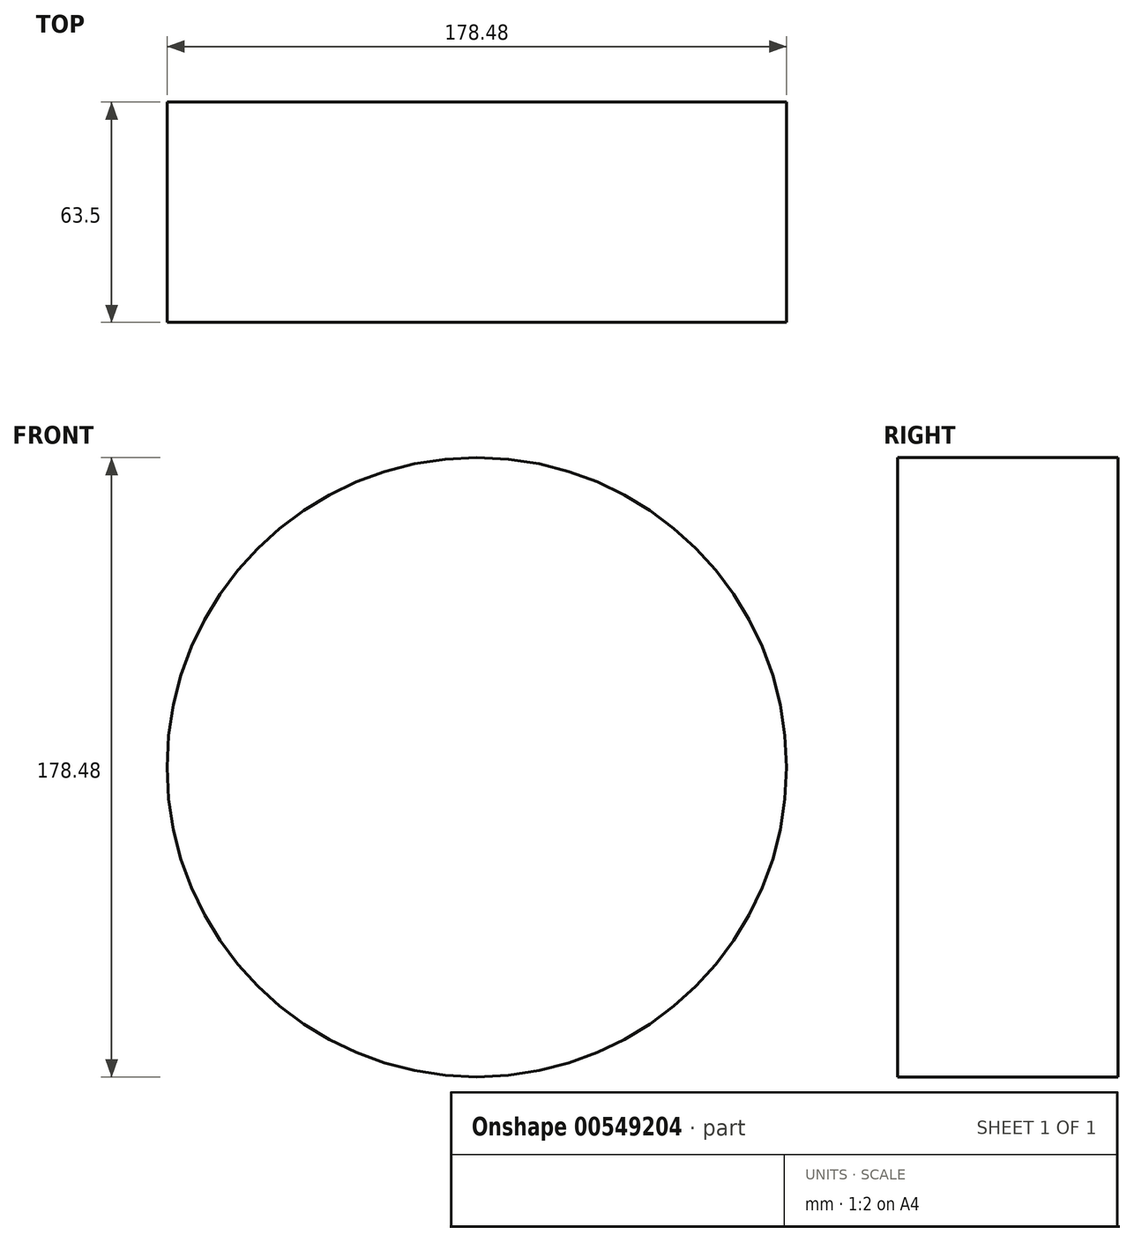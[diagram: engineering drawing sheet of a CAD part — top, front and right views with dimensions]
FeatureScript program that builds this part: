
annotation { "Feature Type Name" : "Feature", "Feature Type Description" : "" }
export const myFeature = defineFeature(function(context is Context, id is Id, definition is map)
    precondition{}
    {
        {
            var Q0;
            Q0=qCreatedBy(makeId("Front.planeOp"),FACE);
            var sketch = newSketch(context, id + "F0", { "sketchPlane" : qUnion([Q0])});
            skCircle(sketch, "E0", {"center": v(0, 0) * mm, "radius": 89.24 * mm});
            skSolve(sketch);
        }
        {
            var Q0;
            Q0=makeQuery(id+"F0.imprint","IMPRINT",FACE,{"disambiguationData":[TD([[makeQuery(id+"F0.imprint","IMPRINT",EDGE,{"derivedFrom":sQuery(id+"F0.wireOp",EDGE,"E0")}),1.0]])]});
            extrude(context, id + "F1", {"entities" : qUnion([Q0]), "depth" : 63.5 * mm, "offsetDistance" : 25.4 * mm});
        }
    });
